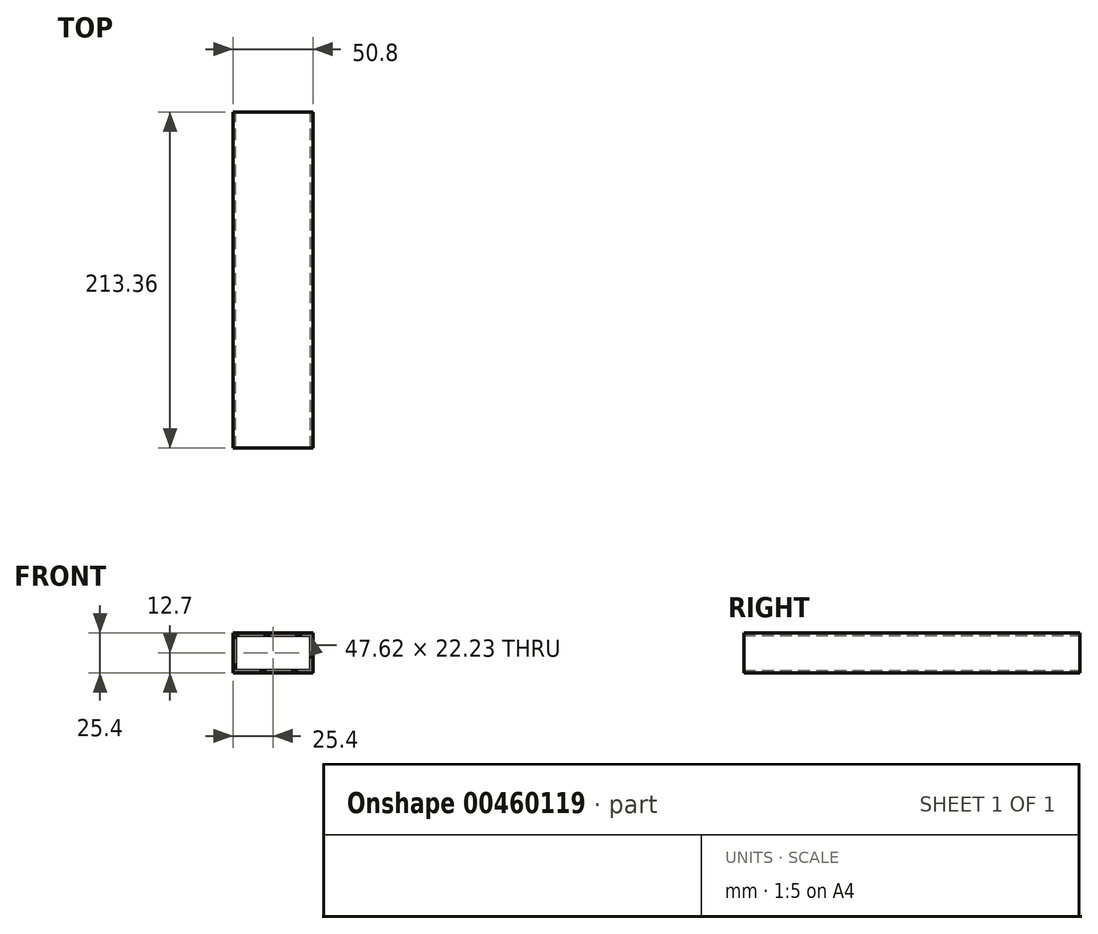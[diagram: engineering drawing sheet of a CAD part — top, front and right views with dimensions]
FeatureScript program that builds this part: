
annotation { "Feature Type Name" : "Feature", "Feature Type Description" : "" }
export const myFeature = defineFeature(function(context is Context, id is Id, definition is map)
    precondition{}
    {
        {
            var Q0;
            Q0=qCreatedBy(makeId("Front.planeOp"),FACE);
            var sketch = newSketch(context, id + "F0", { "sketchPlane" : qUnion([Q0])});
            skLineSegment(sketch, "E0.bottom", {"start": v(25.4, 12.7) * mm, "end": v(-25.4, 12.7) * mm});
            skLineSegment(sketch, "E0.top", {"start": v(25.4, -12.7) * mm, "end": v(-25.4, -12.7) * mm});
            skLineSegment(sketch, "E0.left", {"start": v(25.4, 12.7) * mm, "end": v(25.4, -12.7) * mm});
            skLineSegment(sketch, "E0.right", {"start": v(-25.4, 12.7) * mm, "end": v(-25.4, -12.7) * mm});
            skPoint(sketch, "E0.middle", {"position": v(0, 0) * mm});
            skLineSegment(sketch, "E1.bottom", {"start": v(23.81, 11.11) * mm, "end": v(-23.81, 11.11) * mm});
            skLineSegment(sketch, "E1.top", {"start": v(23.81, -11.11) * mm, "end": v(-23.81, -11.11) * mm});
            skLineSegment(sketch, "E1.left", {"start": v(23.81, 11.11) * mm, "end": v(23.81, -11.11) * mm});
            skLineSegment(sketch, "E1.right", {"start": v(-23.81, 11.11) * mm, "end": v(-23.81, -11.11) * mm});
            skSolve(sketch);
        }
        {
            var Q0;
            Q0=makeQuery(id+"F0.imprint","IMPRINT",FACE,{"disambiguationData":[TD([[makeQuery(id+"F0.imprint","IMPRINT",EDGE,{"derivedFrom":sQuery(id+"F0.wireOp",EDGE,"E0.bottom")}),1.0]])]});
            extrude(context, id + "F1", {"entities" : qUnion([Q0]), "depth" : 213.36 * mm});
        }
    });
